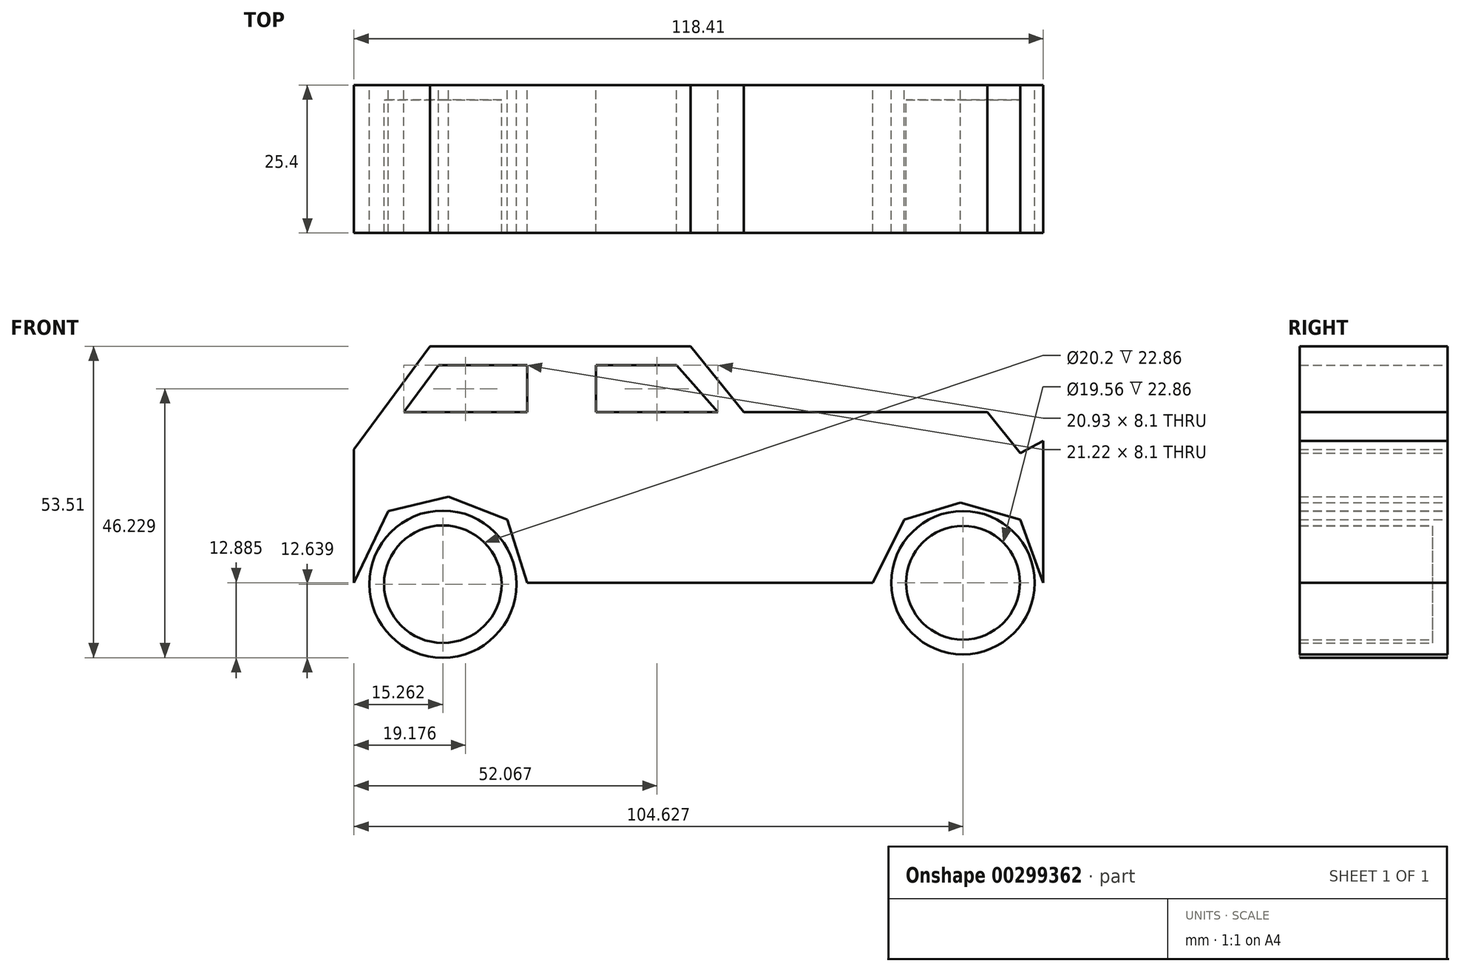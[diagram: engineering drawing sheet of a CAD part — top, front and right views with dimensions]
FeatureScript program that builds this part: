
annotation { "Feature Type Name" : "Feature", "Feature Type Description" : "" }
export const myFeature = defineFeature(function(context is Context, id is Id, definition is map)
    precondition{}
    {
        {
            var Q0;
            Q0=qCreatedBy(makeId("Front.planeOp"),FACE);
            var sketch = newSketch(context, id + "F0", { "sketchPlane" : qUnion([Q0])});
            skLineSegment(sketch, "E0", {"start": v(-30.77, 9.36) * mm, "end": v(28.56, 9.36) * mm});
            skLineSegment(sketch, "E1", {"start": v(-60.56, 9.36) * mm, "end": v(-60.56, 32.25) * mm});
            skLineSegment(sketch, "E2", {"start": v(-60.56, 32.25) * mm, "end": v(-47.51, 49.98) * mm});
            skLineSegment(sketch, "E3", {"start": v(-47.51, 49.98) * mm, "end": v(-2.7, 49.98) * mm});
            skLineSegment(sketch, "E4", {"start": v(-2.7, 49.98) * mm, "end": v(6.4, 38.65) * mm});
            skLineSegment(sketch, "E5", {"start": v(57.85, 9.36) * mm, "end": v(57.85, 33.73) * mm});
            skLineSegment(sketch, "E6", {"start": v(57.85, 33.73) * mm, "end": v(53.92, 36.62) * mm});
            skLineSegment(sketch, "E7", {"start": v(53.92, 36.62) * mm, "end": v(48.25, 38.65) * mm});
            skLineSegment(sketch, "E8", {"start": v(48.25, 38.65) * mm, "end": v(6.4, 38.65) * mm});
            skCircle(sketch, "E9", {"center": v(-45.3, 9.1) * mm, "radius": 12.64 * mm});
            skCircle(sketch, "E10", {"center": v(44.07, 9.36) * mm, "radius": 12.32 * mm});
            skLineSegment(sketch, "E11", {"start": v(-60.56, 9.36) * mm, "end": v(-54.65, 21.66) * mm});
            skLineSegment(sketch, "E12", {"start": v(-54.65, 21.66) * mm, "end": v(-44.31, 24.13) * mm});
            skLineSegment(sketch, "E13", {"start": v(-44.31, 24.13) * mm, "end": v(-34.22, 20.19) * mm});
            skLineSegment(sketch, "E14", {"start": v(-34.22, 20.19) * mm, "end": v(-30.77, 9.36) * mm});
            skLineSegment(sketch, "E15", {"start": v(28.56, 9.36) * mm, "end": v(33.97, 20.19) * mm});
            skLineSegment(sketch, "E16", {"start": v(33.97, 20.19) * mm, "end": v(43.63, 23.15) * mm});
            skLineSegment(sketch, "E17", {"start": v(43.63, 23.15) * mm, "end": v(53.91, 20.19) * mm});
            skLineSegment(sketch, "E18", {"start": v(53.91, 20.19) * mm, "end": v(57.85, 9.36) * mm});
            skLineSegment(sketch, "E19", {"start": v(1.97, 38.65) * mm, "end": v(-5.13, 46.75) * mm});
            skLineSegment(sketch, "E20", {"start": v(-5.13, 46.75) * mm, "end": v(-18.96, 46.75) * mm});
            skLineSegment(sketch, "E21", {"start": v(-18.96, 46.75) * mm, "end": v(-18.96, 38.65) * mm});
            skLineSegment(sketch, "E22", {"start": v(-18.96, 38.65) * mm, "end": v(1.97, 38.65) * mm});
            skLineSegment(sketch, "E23", {"start": v(-30.77, 38.65) * mm, "end": v(-30.77, 46.75) * mm});
            skLineSegment(sketch, "E24", {"start": v(-30.77, 46.75) * mm, "end": v(-46.04, 46.75) * mm});
            skLineSegment(sketch, "E25", {"start": v(-46.04, 46.75) * mm, "end": v(-52, 38.65) * mm});
            skLineSegment(sketch, "E26", {"start": v(-52, 38.65) * mm, "end": v(-30.77, 38.65) * mm});
            skLineSegment(sketch, "E27", {"start": v(48.25, 38.65) * mm, "end": v(53.91, 31.61) * mm});
            skLineSegment(sketch, "E28", {"start": v(53.91, 31.61) * mm, "end": v(57.85, 33.73) * mm});
            skSolve(sketch);
        }
        {
            var Q0;
            Q0=qCreatedBy(makeId("Front.planeOp"),FACE);
            var sketch = newSketch(context, id + "F1", { "sketchPlane" : qUnion([Q0])});
            skSolve(sketch);
        }
        {
            var Q0;
            Q0 = qSketchRegion(id + "F1", true);
            var Q1;
            Q1=makeQuery(id+"F0.imprint","IMPRINT",FACE,{"disambiguationData":[TD([[makeQuery(id+"F0.imprint","IMPRINT",EDGE,{"derivedFrom":sQuery(id+"F0.wireOp",EDGE,"E0")}),1.0]])]});
            var Q2;
            Q2=makeQuery(id+"F0.imprint","IMPRINT",FACE,{"disambiguationData":[TD([[makeQuery(id+"F0.imprint","IMPRINT",EDGE,{"derivedFrom":sQuery(id+"F0.wireOp",EDGE,"E9")}),1.0]])]});
            var Q3;
            Q3=makeQuery(id+"F0.imprint","IMPRINT",FACE,{"disambiguationData":[TD([[makeQuery(id+"F0.imprint","IMPRINT",EDGE,{"derivedFrom":sQuery(id+"F0.wireOp",EDGE,"E10")}),1.0]])]});
            extrude(context, id + "F2", {"entities" : qUnion([Q0, Q1, Q2, Q3]), "depth" : 25.4 * mm});
        }
        {
            var Q0;
            Q0=makeQuery(id+"F2.opExtrude","CAP_FACE",FACE,{"disambiguationData":[OSD([sQuery(id+"F0.wireOp",EDGE,"E9")])],"isStart":false});
            var Q1;
            Q1=makeQuery(id+"F2.opExtrude","CAP_FACE",FACE,{"disambiguationData":[OSD([sQuery(id+"F0.wireOp",EDGE,"E10")])],"isStart":false});
            shell(context, id + "F3", {"entities" : qUnion([Q0, Q1]), "thickness" : 2.54 * mm});
        }
    });
